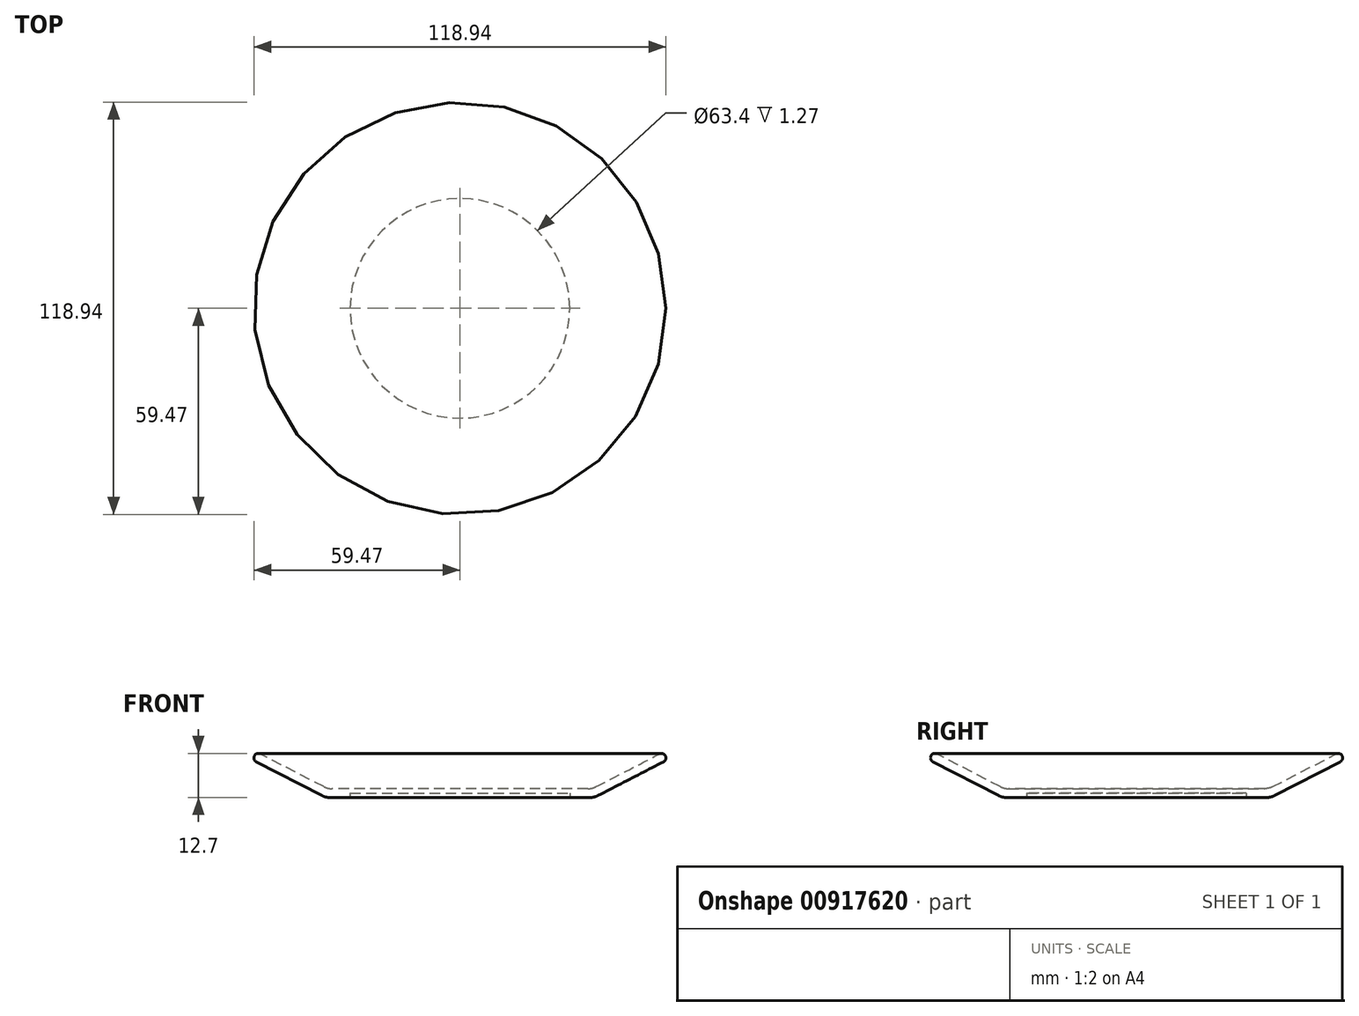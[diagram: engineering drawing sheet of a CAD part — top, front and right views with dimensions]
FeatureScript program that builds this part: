
annotation { "Feature Type Name" : "Feature", "Feature Type Description" : "" }
export const myFeature = defineFeature(function(context is Context, id is Id, definition is map)
    precondition{}
    {
        {
            var Q0;
            Q0=qCreatedBy(makeId("Top.planeOp"),FACE);
            var sketch = newSketch(context, id + "F0", { "sketchPlane" : qUnion([Q0])});
            skCircle(sketch, "E0", {"center": v(0, 0) * mm, "radius": 38.8 * mm});
            skSolve(sketch);
        }
        {
            var Q0;
            Q0=qCreatedBy(makeId("Top.planeOp"),FACE);
            cPlane(context, id + "F1", {"entities" : qUnion([Q0]), "cplaneType" : CPlaneType.OFFSET, "offset" : 12.7 * mm, "width" : 152.4 * mm, "height" : 152.4 * mm});
        }
        {
            var Q0;
            Q0=qCreatedBy(id+"F1.planeOp",FACE);
            var sketch = newSketch(context, id + "F2", { "sketchPlane" : qUnion([Q0])});
            skCircle(sketch, "E1", {"center": v(0, 0) * mm, "radius": 63.43 * mm});
            skSolve(sketch);
        }
        {
            var Q0;
            Q0=makeQuery(id+"F0.imprint","IMPRINT",FACE,{"disambiguationData":[TD([[makeQuery(id+"F0.imprint","IMPRINT",EDGE,{"derivedFrom":sQuery(id+"F0.wireOp",EDGE,"E0")}),1.0]])]});
            var Q1;
            Q1=makeQuery(id+"F2.imprint","IMPRINT",FACE,{"disambiguationData":[TD([[makeQuery(id+"F2.imprint","IMPRINT",EDGE,{"derivedFrom":sQuery(id+"F2.wireOp",EDGE,"E1")}),1.0]])]});
            loft(context, id + "F3", {"sheetProfilesArray" : [{ "sheetProfileEntities" : qUnion([Q0]) }, { "sheetProfileEntities" : qUnion([Q1]) }]});
        }
        {
            var Q0;
            Q0=makeQuery(id+"F3.opLoft","CAP_FACE",FACE,{"disambiguationData":[OSD([makeQuery(id+"F2.imprint","IMPRINT",FACE,{"disambiguationData":[TD([[makeQuery(id+"F2.imprint","IMPRINT",EDGE,{"derivedFrom":sQuery(id+"F2.wireOp",EDGE,"E1")}),1.0]])]})])],"isStart":true});
            shell(context, id + "F4", {"entities" : qUnion([Q0]), "thickness" : 2.54 * mm});
        }
        {
            var Q0;
            Q0=makeQuery(id+"F4.opShell","OFFSET_EDGE",EDGE,{"disambiguationData":[OSD([sQuery(id+"F2.wireOp",EDGE,"E1")])]});
            var Q1;
            Q1=makeQuery(id+"F3.opLoft","MID_CAP_EDGE",EDGE,{"disambiguationData":[OSD([sQuery(id+"F2.wireOp",EDGE,"E1")])],"capPos":1.0});
            fillet(context, id + "F5", {"entities" : qUnion([Q0, Q1]), "radius" : 1.27 * mm, "tangentPropagation" : true, "allowEdgeOverflow" : false});
        }
        {
            var Q0;
            Q0=makeQuery(id+"F3.opLoft","CAP_FACE",FACE,{"disambiguationData":[OSD([makeQuery(id+"F0.imprint","IMPRINT",FACE,{"disambiguationData":[TD([[makeQuery(id+"F0.imprint","IMPRINT",EDGE,{"derivedFrom":sQuery(id+"F0.wireOp",EDGE,"E0")}),1.0]])]})])],"isStart":true});
            var sketch = newSketch(context, id + "F6", { "sketchPlane" : qUnion([Q0])});
            skCircle(sketch, "E2", {"center": v(0, 0) * mm, "radius": 31.7 * mm});
            skSolve(sketch);
        }
        {
            var Q0;
            Q0=makeQuery(id+"F6.imprint","IMPRINT",FACE,{"disambiguationData":[TD([[makeQuery(id+"F6.imprint","IMPRINT",EDGE,{"derivedFrom":sQuery(id+"F6.wireOp",EDGE,"E2")}),1.0]])]});
            extrude(context, id + "F7", {"entities" : qUnion([Q0]), "operationType" : NewBodyOperationType.REMOVE, "oppositeDirection" : true, "depth" : 1.27 * mm, "offsetDistance" : 25.4 * mm});
        }
        {
            var Q0;
            Q0=makeQuery(id+"F7.boolean.opBoolean","COPY",EDGE,{"derivedFrom":makeQuery(id+"F7.opExtrude","CAP_EDGE",EDGE,{"disambiguationData":[OSD([sQuery(id+"F6.wireOp",EDGE,"E2")])],"isStart":true})});
            var Q1;
            Q1=makeQuery(id+"F3.opLoft","MID_CAP_EDGE",EDGE,{"disambiguationData":[OSD([sQuery(id+"F0.wireOp",EDGE,"E0")])],"capPos":0.0});
            fillet(context, id + "F8", {"entities" : qUnion([Q0, Q1]), "radius" : 5.08 * mm, "tangentPropagation" : true, "allowEdgeOverflow" : false});
        }
        {
            var Q0;
            Q0=makeQuery(id+"F4.opShell","OFFSET_EDGE",EDGE,{"disambiguationData":[OSD([sQuery(id+"F0.wireOp",EDGE,"E0")])]});
            fillet(context, id + "F9", {"entities" : qUnion([Q0]), "radius" : 5.08 * mm, "tangentPropagation" : true, "allowEdgeOverflow" : false});
        }
    });
